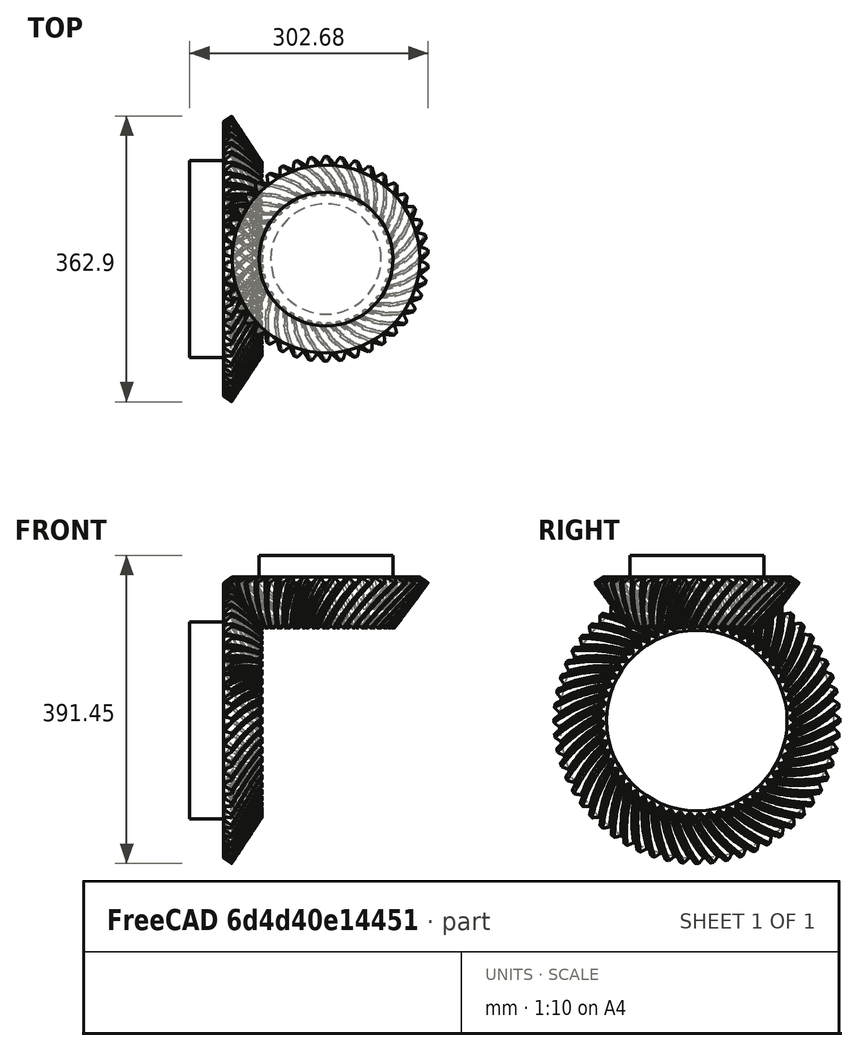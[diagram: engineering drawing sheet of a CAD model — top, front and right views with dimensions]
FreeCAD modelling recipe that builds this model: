
FCSTD DOCUMENT  (FreeCAD 0.18R14555 (Git shallow))
Label: FREECAD #45 - ENGRENAGEM CONICA
License: All rights reserved
LicenseURL: http://en.wikipedia.org/wiki/All_rights_reserved
objects: Part::Cut×6, Part::Cone×4, Part::Cylinder×4, Part::FeaturePython×2, Part::MultiFuse×2
note: 18 computed .brp shape members not serialized (recipe doc carries the construction recipe); baked Part::Feature solids carry a one-line shape summary decoded from their .brp

FEATURE [Part::FeaturePython] BevelGear  # WARN: FeaturePython — macro-defined, semantics opaque (R4)
  backlash = 0
  beta = 20
  clearance = 0.1
  height = 50
  m = 5
  numpoints = 6
  pitch_angle = 55
  pressure_angle = 20
  teeth = 60
FEATURE [Part::Cone] Cone
  Angle = 360
  AttacherType = Attacher::AttachEngine3D
  Height = 270
  Radius1 = 175
  Radius2 = 0
FEATURE [Part::Cut] Cut
  Base = -> BevelGear
  Tool = -> Cone
FEATURE [Part::Cone] Cone001
  Angle = 360
  AttacherType = Attacher::AttachEngine3D
  Height = 380
  Radius1 = 265
  Radius2 = 0
FEATURE [Part::Cylinder] Cylinder  label="Cilindro"
  Angle = 360
  AttacherType = Attacher::AttachEngine3D
  Height = 200
  Radius = 300
FEATURE [Part::Cut] Cut001
  Base = -> Cylinder
  Tool = -> Cone001
FEATURE [Part::Cut] Cut002
  Base = -> Cut
  Tool = -> Cut001
FEATURE [Part::Cylinder] Cylinder001  label="Cilindro001"
  Angle = 360
  AttacherType = Attacher::AttachEngine3D
  Height = 80
  Placement = pos=(0,0,93) rot=(0,0,1;0rad)
  Radius = 125
FEATURE [Part::MultiFuse] Fusion
  Placement = pos=(0,0,0) rot=(0,-1,0;1.5708rad)
  Shapes = -> [Cut002,Cylinder001]
FEATURE [Part::FeaturePython] BevelGear001  # WARN: FeaturePython — macro-defined, semantics opaque (R4)
  backlash = 0
  beta = -40
  clearance = 0.1
  height = 65
  m = 5
  numpoints = 6
  pitch_angle = 35
  pressure_angle = 20
  teeth = 42
FEATURE [Part::Cone] Cone002
  Angle = 360
  AttacherType = Attacher::AttachEngine3D
  Height = 179
  Radius1 = 256
  Radius2 = 0
FEATURE [Part::Cut] Cut003
  Base = -> BevelGear001
  Tool = -> Cone002
FEATURE [Part::Cone] Cone003
  Angle = 360
  AttacherType = Attacher::AttachEngine3D
  Height = 266
  Radius1 = 380
  Radius2 = 0
FEATURE [Part::Cylinder] Cylinder002  label="Cilindro002"
  Angle = 360
  AttacherType = Attacher::AttachEngine3D
  Height = 200
  Radius = 200
FEATURE [Part::Cut] Cut004
  Base = -> Cylinder002
  Tool = -> Cone003
FEATURE [Part::Cut] Cut005
  Base = -> Cut003
  Tool = -> Cut004
FEATURE [Part::Cylinder] Cylinder003  label="Cilindro003"
  Angle = 360
  AttacherType = Attacher::AttachEngine3D
  Height = 80
  Placement = pos=(0,0,130) rot=(0,0,1;0rad)
  Radius = 85
FEATURE [Part::MultiFuse] Fusion001
  Placement = pos=(0,0,0) rot=(0,0,1;0.277507rad)
  Shapes = -> [Cut005,Cylinder003]
